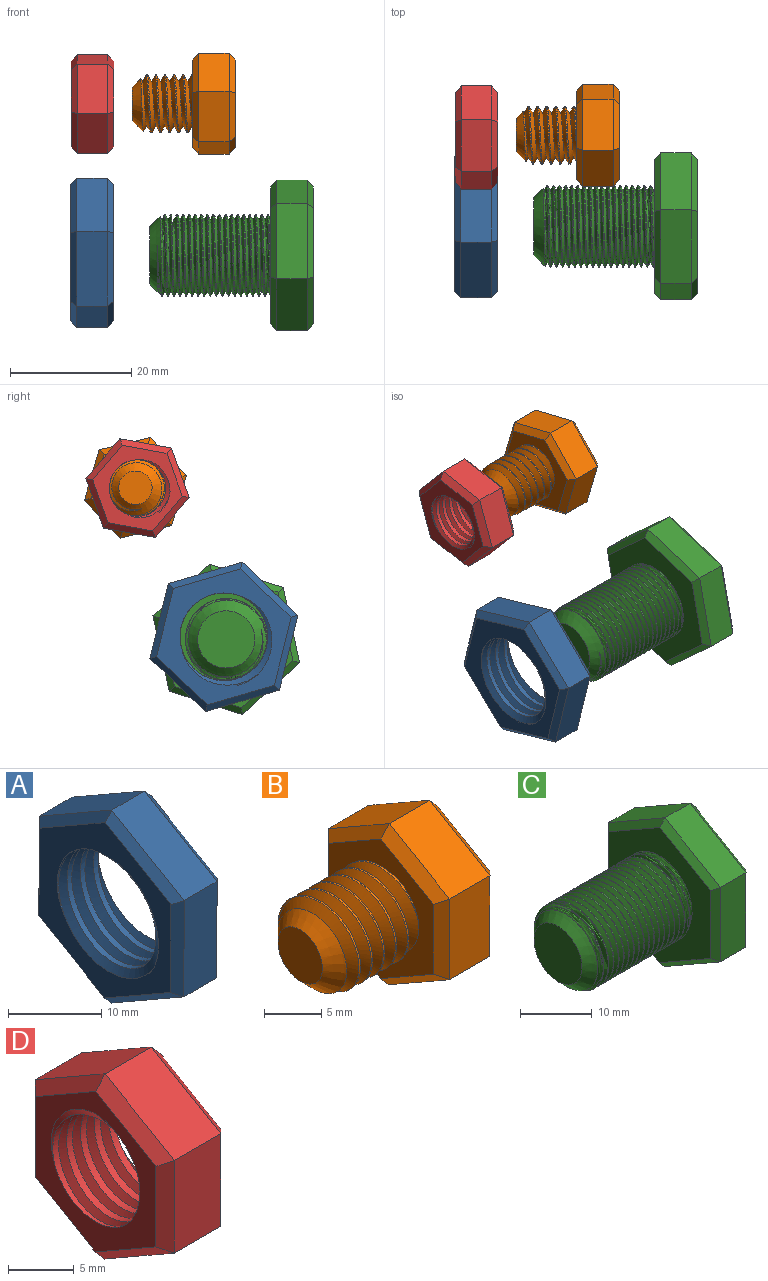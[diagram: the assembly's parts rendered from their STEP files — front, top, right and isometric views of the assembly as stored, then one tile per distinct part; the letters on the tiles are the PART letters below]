
ASSEMBLY  parts=4 mates=2
PART A: 23 faces, bbox 9.3x22.7x26 mm
  f0: cylinder r=7.24mm len=14.48mm, axis (1,0,0), area 111.6mm2, adj f7,f8,f21,f22
  f1: plane 10.98x6.38mm, normal (0,-0.5,0.86), area 63.5mm2, adj f2,f6,f14,f18
  f2: plane 12.7x5mm, normal (0,-1,0), area 63.5mm2, adj f1,f3,f12,f16
  f3: plane 11.02x6.32mm, normal (0,-0.5,-0.87), area 63.5mm2, adj f2,f4,f10,f15
  f4: plane 10.98x6.38mm, normal (0,0.5,-0.86), area 63.5mm2, adj f3,f5,f9,f17
  f5: plane 12.7x5mm, normal (0,1,0), area 63.5mm2, adj f4,f6,f11,f19
  f6: plane 11.02x6.32mm, normal (0,0.5,0.87), area 63.5mm2, adj f1,f5,f13,f20
  f7: plane 23.73x20.67mm, normal (-1,0,0), area 164.4mm2, adj f0,f9,f10,f11,f12,f13,f14,f21
  f8: plane 23.73x20.67mm, normal (1,0,0), area 164.4mm2, adj f0,f15,f16,f17,f18,f19,f20,f21
  f9: plane 10.99x6.96mm, normal (-0.71,0.36,-0.61), area 17.1mm2, adj f4,f7,f10,f11
  f10: plane 11.02x6.9mm, normal (-0.71,-0.35,-0.61), area 17.1mm2, adj f3,f7,f9,f12
  f11: plane 12.7x1.03mm, normal (-0.71,0.71,0), area 17.1mm2, adj f5,f7,f9,f13
  f12: plane 12.7x1.03mm, normal (-0.71,-0.71,0), area 17.1mm2, adj f2,f7,f10,f14
  f13: plane 11.02x6.9mm, normal (-0.71,0.35,0.61), area 17.1mm2, adj f6,f7,f11,f14
  f14: plane 10.99x6.96mm, normal (-0.71,-0.36,0.61), area 17.1mm2, adj f1,f7,f12,f13
  f15: plane 11.02x6.9mm, normal (0.71,-0.35,-0.61), area 17.1mm2, adj f3,f8,f16,f17
  f16: plane 12.7x1.03mm, normal (0.71,-0.71,0), area 17.1mm2, adj f2,f8,f15,f18
  f17: plane 10.99x6.96mm, normal (0.71,0.36,-0.61), area 17.1mm2, adj f4,f8,f15,f19
  f18: plane 10.99x6.96mm, normal (0.71,-0.36,0.61), area 17.1mm2, adj f1,f8,f16,f20
  f19: plane 12.7x1.03mm, normal (0.71,0.71,0), area 17.1mm2, adj f5,f8,f17,f20
  f20: plane 11.02x6.9mm, normal (0.71,0.35,0.61), area 17.1mm2, adj f6,f8,f18,f19
  f21: bspline ~19.31x16.73mm, area 223mm2, adj f0,f7,f8,f22
  f22: bspline ~19.31x16.73mm, area 223mm2, adj f0,f7,f8,f21
PART B: 25 faces, bbox 17.8x15.9x18.1 mm
  f0: cylinder r=4.75mm len=9.5mm, axis (1,0,0), area 28.1mm2, adj f1,f2,f4,f12
  f1: bspline ~10.97x9.91mm, area 196.7mm2, adj f0,f2,f4,f12
  f2: bspline ~10.97x10.66mm, area 196.6mm2, adj f0,f1,f4,f12
  f3: plane 5.5x5.5mm, normal (-1,0,0), area 23.8mm2, adj f4
  f4: cone r=4.75mm half-angle=45deg, axis (1,0,0), area 47.4mm2, adj f0,f1,f2,f3
  f5: plane 7.48x5mm, normal (0,-0.5,0.86), area 43.3mm2, adj f6,f10,f18,f22
  f6: plane 8.66x5mm, normal (0,-1,0), area 43.3mm2, adj f5,f7,f16,f20
  f7: plane 7.52x5mm, normal (0,-0.5,-0.87), area 43.3mm2, adj f6,f8,f14,f19
  f8: plane 7.48x5mm, normal (0,0.5,-0.86), area 43.3mm2, adj f7,f9,f13,f21
  f9: plane 8.66x5mm, normal (0,1,0), area 43.3mm2, adj f8,f10,f15,f23
  f10: plane 7.52x5mm, normal (0,0.5,0.87), area 43.3mm2, adj f5,f9,f17,f24
  f11: plane 15.01x13.03mm, normal (1,0,0), area 146.4mm2, adj f13,f14,f15,f16,f17,f18
  f12: plane 15.83x13.85mm, normal (-1,0,0), area 89.2mm2, adj f0,f1,f2,f19,f20,f21,f22,f23
  f13: plane 7.49x4.93mm, normal (0.71,0.36,-0.61), area 11.4mm2, adj f8,f11,f14,f15
  f14: plane 7.52x4.88mm, normal (0.71,-0.35,-0.61), area 11.4mm2, adj f7,f11,f13,f16
  f15: plane 8.66x1.03mm, normal (0.71,0.71,0), area 11.4mm2, adj f9,f11,f13,f17
  f16: plane 8.66x1.03mm, normal (0.71,-0.71,0), area 11.4mm2, adj f6,f11,f14,f18
  f17: plane 7.52x4.88mm, normal (0.71,0.35,0.61), area 11.4mm2, adj f10,f11,f15,f18
  f18: plane 7.49x4.93mm, normal (0.71,-0.36,0.61), area 11.4mm2, adj f5,f11,f16,f17
  f19: plane 7.52x4.88mm, normal (-0.71,-0.35,-0.61), area 11.4mm2, adj f7,f12,f20,f21
  f20: plane 8.66x1.03mm, normal (-0.71,-0.71,0), area 11.4mm2, adj f6,f12,f19,f22
  f21: plane 7.49x4.93mm, normal (-0.71,0.36,-0.61), area 11.4mm2, adj f8,f12,f19,f23
  f22: plane 7.49x4.93mm, normal (-0.71,-0.36,0.61), area 11.4mm2, adj f5,f12,f20,f24
  f23: plane 8.66x1.03mm, normal (-0.71,0.71,0), area 11.4mm2, adj f9,f12,f21,f24
  f24: plane 7.52x4.88mm, normal (-0.71,0.35,0.61), area 11.4mm2, adj f10,f12,f22,f23
PART C: 25 faces, bbox 28x22.6x26 mm
  f0: cylinder r=6.72mm len=18mm, axis (1,0,0), area 114.6mm2, adj f1,f2,f4,f12
  f1: bspline ~19.44x15.52mm, area 641.4mm2, adj f0,f2,f4,f12
  f2: bspline ~20.94x15.52mm, area 631.3mm2, adj f0,f1,f4,f12
  f3: plane 9.44x9.44mm, normal (-1,0,0), area 70mm2, adj f4
  f4: cone r=6.72mm half-angle=45deg, axis (1,0,0), area 82.6mm2, adj f0,f1,f2,f3
  f5: plane 10.98x6.39mm, normal (0,-0.5,0.86), area 63.5mm2, adj f6,f10,f18,f22
  f6: plane 12.7x5mm, normal (0,-1,0), area 63.5mm2, adj f5,f7,f16,f20
  f7: plane 11.02x6.31mm, normal (0,-0.5,-0.87), area 63.5mm2, adj f6,f8,f14,f19
  f8: plane 10.98x6.39mm, normal (0,0.5,-0.86), area 63.5mm2, adj f7,f9,f13,f21
  f9: plane 12.7x5mm, normal (0,1,0), area 63.5mm2, adj f8,f10,f15,f23
  f10: plane 11.02x6.31mm, normal (0,0.5,0.87), area 63.5mm2, adj f5,f9,f17,f24
  f11: plane 23.09x20.04mm, normal (1,0,0), area 346.4mm2, adj f13,f14,f15,f16,f17,f18
  f12: plane 23.69x20.63mm, normal (-1,0,0), area 218mm2, adj f0,f1,f2,f19,f20,f21,f22,f23
  f13: plane 10.98x6.96mm, normal (0.71,0.36,-0.61), area 17.1mm2, adj f8,f11,f14,f15
  f14: plane 11.02x6.9mm, normal (0.71,-0.35,-0.61), area 17.1mm2, adj f7,f11,f13,f16
  f15: plane 12.7x1.04mm, normal (0.71,0.71,0), area 17.1mm2, adj f9,f11,f13,f17
  f16: plane 12.7x1.04mm, normal (0.71,-0.71,0), area 17.1mm2, adj f6,f11,f14,f18
  f17: plane 11.02x6.9mm, normal (0.71,0.35,0.61), area 17.1mm2, adj f10,f11,f15,f18
  f18: plane 10.98x6.96mm, normal (0.71,-0.36,0.61), area 17.1mm2, adj f5,f11,f16,f17
  f19: plane 11.02x6.9mm, normal (-0.71,-0.35,-0.61), area 17.1mm2, adj f7,f12,f20,f21
  f20: plane 12.7x1.04mm, normal (-0.71,-0.71,0), area 17.1mm2, adj f6,f12,f19,f22
  f21: plane 10.98x6.96mm, normal (-0.71,0.36,-0.61), area 17.1mm2, adj f8,f12,f19,f23
  f22: plane 10.98x6.96mm, normal (-0.71,-0.36,0.61), area 17.1mm2, adj f5,f12,f20,f24
  f23: plane 12.7x1.04mm, normal (-0.71,0.71,0), area 17.1mm2, adj f9,f12,f21,f24
  f24: plane 11.02x6.9mm, normal (-0.71,0.35,0.61), area 17.1mm2, adj f10,f12,f22,f23
PART D: 23 faces, bbox 9.1x15.4x17.7 mm
  f0: plane 7.49x5mm, normal (0,-0.5,0.86), area 43.3mm2, adj f1,f5,f13,f17
  f1: plane 8.66x5mm, normal (0,-1,0), area 43.3mm2, adj f0,f2,f11,f15
  f2: plane 7.51x5mm, normal (0,-0.5,-0.87), area 43.3mm2, adj f1,f3,f9,f14
  f3: plane 7.49x5mm, normal (0,0.5,-0.86), area 43.3mm2, adj f2,f4,f8,f16
  f4: plane 8.66x5mm, normal (0,1,0), area 43.3mm2, adj f3,f5,f10,f18
  f5: plane 7.51x5mm, normal (0,0.5,0.87), area 43.3mm2, adj f0,f4,f12,f19
  f6: plane 15.37x13.38mm, normal (-1,0,0), area 71.4mm2, adj f8,f9,f10,f11,f12,f13,f20,f21
  f7: plane 15.37x13.38mm, normal (1,0,0), area 71.4mm2, adj f14,f15,f16,f17,f18,f19,f20,f21
  f8: plane 7.49x4.93mm, normal (-0.71,0.36,-0.61), area 11.4mm2, adj f3,f6,f9,f10
  f9: plane 7.51x4.89mm, normal (-0.71,-0.35,-0.61), area 11.4mm2, adj f2,f6,f8,f11
  f10: plane 8.66x1.02mm, normal (-0.71,0.71,0), area 11.4mm2, adj f4,f6,f8,f12
  f11: plane 8.66x1.02mm, normal (-0.71,-0.71,0), area 11.4mm2, adj f1,f6,f9,f13
  f12: plane 7.51x4.89mm, normal (-0.71,0.35,0.61), area 11.4mm2, adj f5,f6,f10,f13
  f13: plane 7.49x4.93mm, normal (-0.71,-0.36,0.61), area 11.4mm2, adj f0,f6,f11,f12
  f14: plane 7.51x4.89mm, normal (0.71,-0.35,-0.61), area 11.4mm2, adj f2,f7,f15,f16
  f15: plane 8.66x1.02mm, normal (0.71,-0.71,0), area 11.4mm2, adj f1,f7,f14,f17
  f16: plane 7.49x4.93mm, normal (0.71,0.36,-0.61), area 11.4mm2, adj f3,f7,f14,f18
  f17: plane 7.49x4.93mm, normal (0.71,-0.36,0.61), area 11.4mm2, adj f0,f7,f15,f19
  f18: plane 8.66x1.02mm, normal (0.71,0.71,0), area 11.4mm2, adj f4,f7,f16,f19
  f19: plane 7.51x4.89mm, normal (0.71,0.35,0.61), area 11.4mm2, adj f5,f7,f17,f18
  f20: cylinder r=4.66mm len=9.32mm, axis (1,0,0), area 85.4mm2, adj f6,f7,f21,f22
  f21: bspline ~12.5x10.82mm, area 128.4mm2, adj f6,f7,f20,f22
  f22: bspline ~12.5x10.82mm, area 128.5mm2, adj f6,f7,f20,f21
PLACE A rot(axis=(0,0.6,-0.8),180deg) t=(-55.27,-6.86,23.48)mm fixed
PLACE B rot(axis=(-1,0,0),43.8deg) t=(-31.66,7.73,48.08)mm
PLACE C rot(axis=(1,0,0),167.5deg) t=(-18.77,-7.25,23.06)mm
PLACE D rot(axis=(1,0,0),100.2deg) t=(-48.16,7.38,48.02)mm fixed
MATE cylindrical C.f0 <-> A.f7  axis (-1,0,0) through (-42.27,-7.25,23.06)mm
MATE cylindrical B.f0 <-> D.f6  axis (-1,0,0) through (-45.16,7.73,48.08)mm
